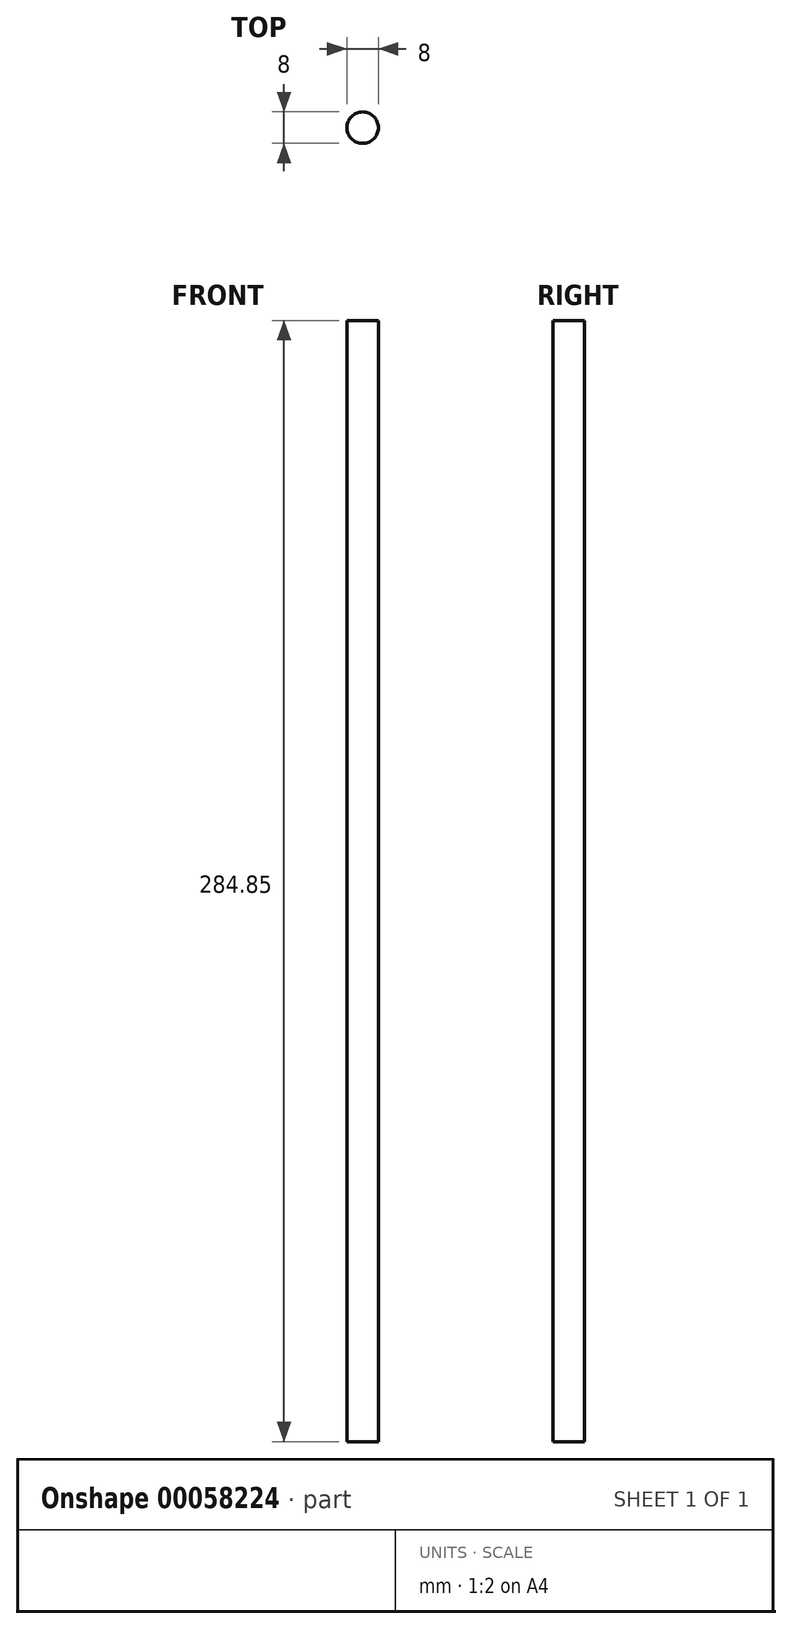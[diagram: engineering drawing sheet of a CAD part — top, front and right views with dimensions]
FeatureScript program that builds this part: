
annotation { "Feature Type Name" : "Feature", "Feature Type Description" : "" }
export const myFeature = defineFeature(function(context is Context, id is Id, definition is map)
    precondition{}
    {
        {
            var Q0;
            Q0=qCreatedBy(makeId("Top.planeOp"),FACE);
            var sketch = newSketch(context, id + "F0", { "sketchPlane" : qUnion([Q0])});
            skCircle(sketch, "E0", {"center": v(0, 0) * mm, "radius": 4 * mm});
            skSolve(sketch);
        }
        {
            var Q0;
            Q0 = qSketchRegion(id + "F0", true);
            extrude(context, id + "F1", {"entities" : qUnion([Q0]), "depth" : 284.85 * mm});
        }
    });
